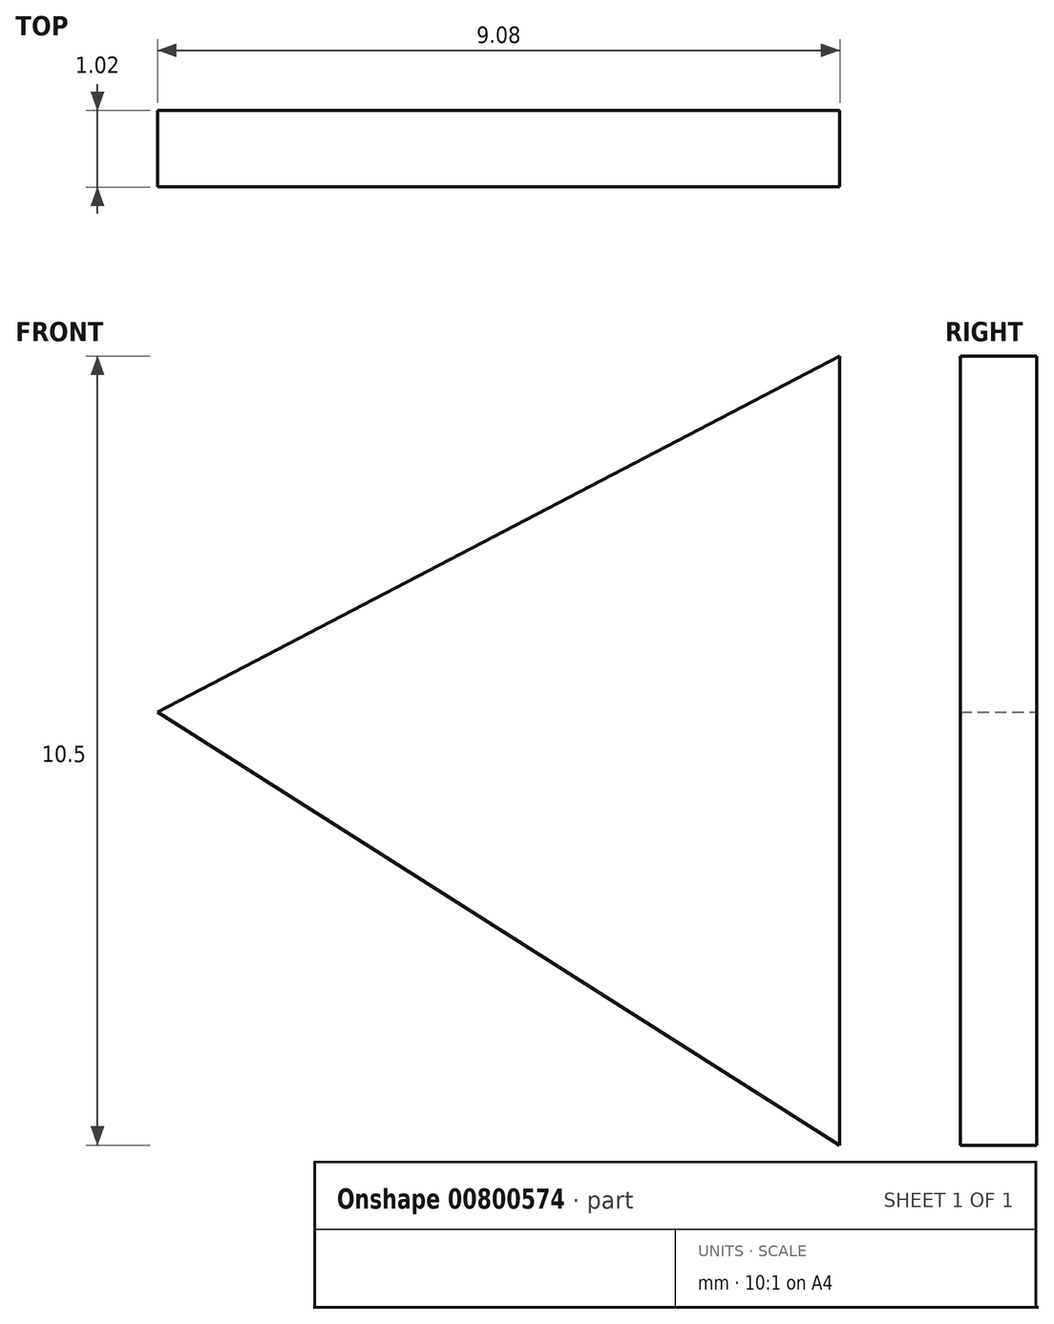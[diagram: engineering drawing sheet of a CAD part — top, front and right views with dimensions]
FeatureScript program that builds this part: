
annotation { "Feature Type Name" : "Feature", "Feature Type Description" : "" }
export const myFeature = defineFeature(function(context is Context, id is Id, definition is map)
    precondition{}
    {
        {
            var Q0;
            Q0=qCreatedBy(makeId("Front.planeOp"),FACE);
            var sketch = newSketch(context, id + "F0", { "sketchPlane" : qUnion([Q0])});
            skLineSegment(sketch, "E0", {"start": v(-6.05, 0.35) * mm, "end": v(3.03, 5.08) * mm});
            skLineSegment(sketch, "E1", {"start": v(3.03, 5.08) * mm, "end": v(3.03, -5.42) * mm});
            skLineSegment(sketch, "E2", {"start": v(3.03, -5.42) * mm, "end": v(-6.05, 0.35) * mm});
            skSolve(sketch);
        }
        {
            var Q0;
            Q0=makeQuery(id+"F0.imprint","IMPRINT",FACE,{"disambiguationData":[TD([[makeQuery(id+"F0.imprint","IMPRINT",EDGE,{"derivedFrom":sQuery(id+"F0.wireOp",EDGE,"E0")}),-1.0]])]});
            var Q1;
            Q1=sQuery(id+"F0.wireOp",EDGE,"E0");
            var Q2;
            Q2=sQuery(id+"F0.wireOp",EDGE,"E1");
            var Q3;
            Q3=sQuery(id+"F0.wireOp",EDGE,"E2");
            extrude(context, id + "F1", {"entities" : qUnion([Q0]), "surfaceEntities" : qUnion([Q1, Q2, Q3]), "depth" : 1.02 * mm, "offsetDistance" : 25.4 * mm});
        }
    });
